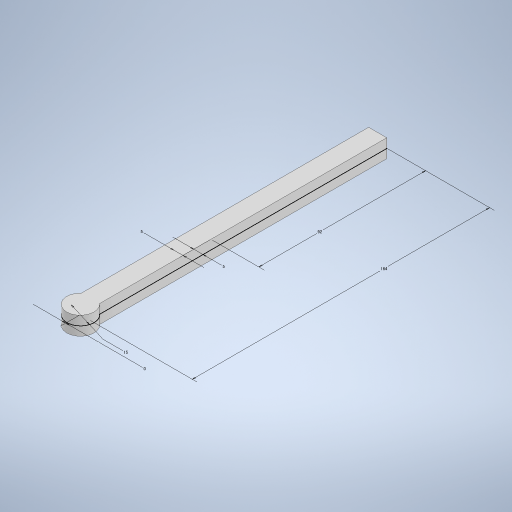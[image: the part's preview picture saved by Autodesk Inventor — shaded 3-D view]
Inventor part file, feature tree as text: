
AUTODESK INVENTOR PART (.ipt)
format: ipt  version: 2024.3 (Build 283343000, 343)  size: 253,440 bytes
history: native  units: mm
features: other x1, sketch x1, extrude x1
ambient origin geometry x8: Origin, YZ Plane, XZ Plane, XY Plane, X Axis, Y Axis, Z Axis, Center Point
bodies: Body1 (feature_tree)
feature tree (3):
  other  "ソリッド1"
  sketch  "スケッチ1"
  extrude  "押し出し1"  Depth=15.0mm
